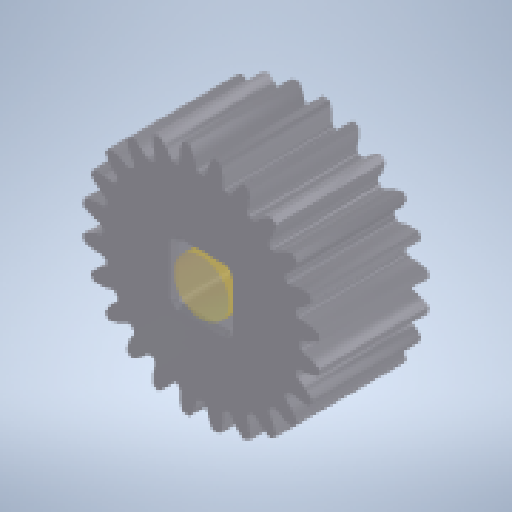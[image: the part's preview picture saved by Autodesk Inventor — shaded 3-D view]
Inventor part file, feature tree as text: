
AUTODESK INVENTOR PART (.ipt)
format: ipt  version: 2025.2 (Build 292293000, 293)  size: 356,864 bytes
history: native  units: in
note: dims shown in document units (in); Inventor stores cm internally (conversion verified against a paired STEP export)
features: other x1, chamfer x1, extrude x1
ambient origin geometry x8: Origin, YZ Plane, XZ Plane, XY Plane, X Axis, Y Axis, Z Axis, Center Point
bodies: Solid1 (feature_tree)
feature tree (3):
  other  "Srf1"
  chamfer  "Chamfer1"  Distance=0.25in
  extrude  "ExtrusionSrf1"  Depth=0.25in TaperAngle=0.0deg
